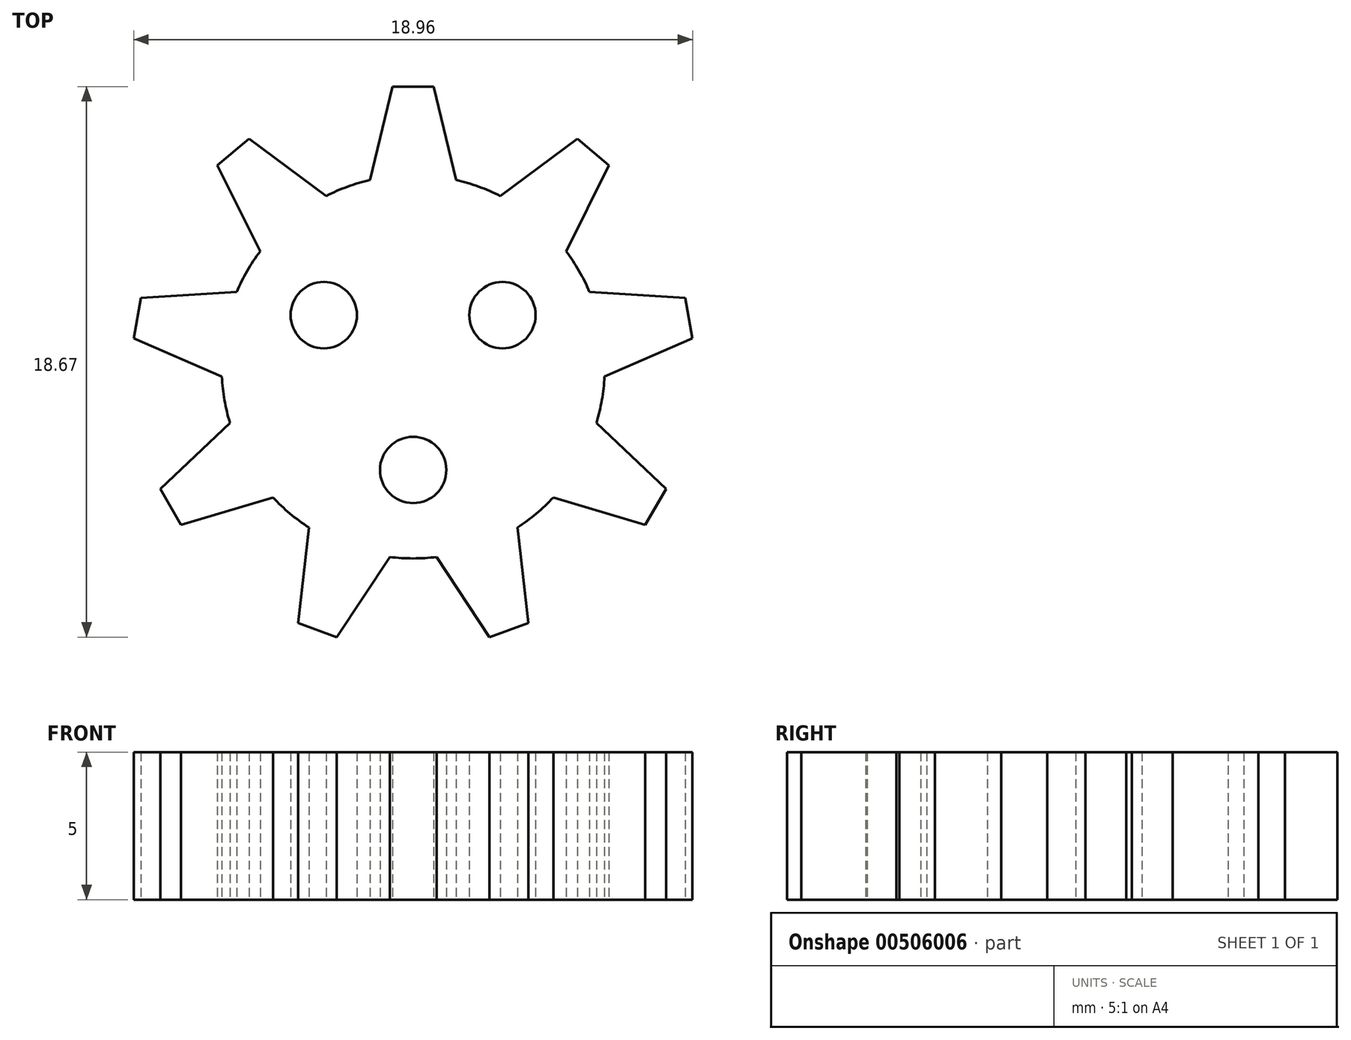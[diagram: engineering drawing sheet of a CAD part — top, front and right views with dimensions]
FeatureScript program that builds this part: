
annotation { "Feature Type Name" : "Feature", "Feature Type Description" : "" }
export const myFeature = defineFeature(function(context is Context, id is Id, definition is map)
    precondition{}
    {
        {
            var Q0;
            Q0=qCreatedBy(makeId("Top.planeOp"),FACE);
            var sketch = newSketch(context, id + "F0", { "sketchPlane" : qUnion([Q0])});
            skCircle(sketch, "E0", {"center": v(0, 0) * mm, "radius": 6.5 * mm});
            skLineSegment(sketch, "E1", {"start": v(0, 6.5) * mm, "end": v(0, 9.5) * mm});
            skLineSegment(sketch, "E2", {"start": v(0, 9.5) * mm, "end": v(0.7, 9.5) * mm});
            skLineSegment(sketch, "E3", {"start": v(0.7, 9.5) * mm, "end": v(1.46, 6.33) * mm});
            skLineSegment(sketch, "E4.MirrorCS", {"start": v(0, 9.5) * mm, "end": v(-0.7, 9.5) * mm});
            skLineSegment(sketch, "E5.MirrorCS", {"start": v(-0.7, 9.5) * mm, "end": v(-1.46, 6.33) * mm});
            skLineSegment(sketch, "E6.1.0", {"start": v(-6.64, 6.83) * mm, "end": v(-5.19, 3.91) * mm});
            skLineSegment(sketch, "E6.1.1", {"start": v(-6.1, 7.28) * mm, "end": v(-6.64, 6.83) * mm});
            skLineSegment(sketch, "E6.1.2", {"start": v(-6.1, 7.28) * mm, "end": v(-5.57, 7.73) * mm});
            skLineSegment(sketch, "E6.1.3", {"start": v(-5.57, 7.73) * mm, "end": v(-2.95, 5.8) * mm});
            skLineSegment(sketch, "E6.2.0", {"start": v(-9.48, 0.96) * mm, "end": v(-6.5, -0.34) * mm});
            skLineSegment(sketch, "E6.2.1", {"start": v(-9.36, 1.65) * mm, "end": v(-9.48, 0.96) * mm});
            skLineSegment(sketch, "E6.2.2", {"start": v(-9.36, 1.65) * mm, "end": v(-9.23, 2.34) * mm});
            skLineSegment(sketch, "E6.2.3", {"start": v(-9.23, 2.34) * mm, "end": v(-5.98, 2.54) * mm});
            skLineSegment(sketch, "E6.3.0", {"start": v(-7.88, -5.36) * mm, "end": v(-4.76, -4.43) * mm});
            skLineSegment(sketch, "E6.3.1", {"start": v(-8.23, -4.75) * mm, "end": v(-7.88, -5.36) * mm});
            skLineSegment(sketch, "E6.3.2", {"start": v(-8.23, -4.75) * mm, "end": v(-8.58, -4.14) * mm});
            skLineSegment(sketch, "E6.3.3", {"start": v(-8.58, -4.14) * mm, "end": v(-6.22, -1.9) * mm});
            skLineSegment(sketch, "E6.4.0", {"start": v(-2.6, -9.17) * mm, "end": v(-0.8, -6.45) * mm});
            skLineSegment(sketch, "E6.4.1", {"start": v(-3.25, -8.93) * mm, "end": v(-2.6, -9.17) * mm});
            skLineSegment(sketch, "E6.4.2", {"start": v(-3.25, -8.93) * mm, "end": v(-3.9, -8.69) * mm});
            skLineSegment(sketch, "E6.4.3", {"start": v(-3.9, -8.69) * mm, "end": v(-3.54, -5.45) * mm});
            skLineSegment(sketch, "E6.5.0", {"start": v(3.9, -8.69) * mm, "end": v(3.54, -5.45) * mm});
            skLineSegment(sketch, "E6.5.1", {"start": v(3.25, -8.93) * mm, "end": v(3.9, -8.69) * mm});
            skLineSegment(sketch, "E6.5.2", {"start": v(3.25, -8.93) * mm, "end": v(2.6, -9.17) * mm});
            skLineSegment(sketch, "E6.5.3", {"start": v(2.6, -9.17) * mm, "end": v(0.8, -6.45) * mm});
            skLineSegment(sketch, "E6.6.0", {"start": v(8.58, -4.14) * mm, "end": v(6.22, -1.9) * mm});
            skLineSegment(sketch, "E6.6.1", {"start": v(8.23, -4.75) * mm, "end": v(8.58, -4.14) * mm});
            skLineSegment(sketch, "E6.6.2", {"start": v(8.23, -4.75) * mm, "end": v(7.88, -5.36) * mm});
            skLineSegment(sketch, "E6.6.3", {"start": v(7.88, -5.36) * mm, "end": v(4.76, -4.43) * mm});
            skLineSegment(sketch, "E6.7.0", {"start": v(9.23, 2.34) * mm, "end": v(5.98, 2.54) * mm});
            skLineSegment(sketch, "E6.7.1", {"start": v(9.36, 1.65) * mm, "end": v(9.23, 2.34) * mm});
            skLineSegment(sketch, "E6.7.2", {"start": v(9.36, 1.65) * mm, "end": v(9.48, 0.96) * mm});
            skLineSegment(sketch, "E6.7.3", {"start": v(9.48, 0.96) * mm, "end": v(6.5, -0.34) * mm});
            skLineSegment(sketch, "E6.8.0", {"start": v(5.57, 7.73) * mm, "end": v(2.95, 5.8) * mm});
            skLineSegment(sketch, "E6.8.1", {"start": v(6.1, 7.28) * mm, "end": v(5.57, 7.73) * mm});
            skLineSegment(sketch, "E6.8.2", {"start": v(6.1, 7.28) * mm, "end": v(6.64, 6.83) * mm});
            skLineSegment(sketch, "E6.8.3", {"start": v(6.64, 6.83) * mm, "end": v(5.19, 3.91) * mm});
            skLineSegment(sketch, "E7", {"start": v(0, 0) * mm, "end": v(0, -3.5) * mm});
            skCircle(sketch, "E8", {"center": v(0, -3.5) * mm, "radius": 1.13 * mm});
            skCircle(sketch, "E9.1.0", {"center": v(3.03, 1.75) * mm, "radius": 1.13 * mm});
            skCircle(sketch, "E9.2.0", {"center": v(-3.03, 1.75) * mm, "radius": 1.13 * mm});
            skSolve(sketch);
        }
        {
            var Q0;
            Q0=makeQuery(id+"F0.imprint","IMPRINT",FACE,{"disambiguationData":[TD([[makeQuery(id+"F0.imprint","IMPRINT",EDGE,{"derivedFrom":sQuery(id+"F0.wireOp",EDGE,"E8")}),-1.0]])]});
            var Q1;
            {var subQ0=sQuery(id+"F0.wireOp",EDGE,"E6.4.0");Q1=makeQuery(id+"F0.imprint","IMPRINT",FACE,{"disambiguationData":[TD([[makeQuery(id+"F0.imprint","IMPRINT",EDGE,{"derivedFrom":subQ0}),1.0]])]});}
            var Q2;
            {var subQ0=sQuery(id+"F0.wireOp",EDGE,"E6.5.0");Q2=makeQuery(id+"F0.imprint","IMPRINT",FACE,{"disambiguationData":[TD([[makeQuery(id+"F0.imprint","IMPRINT",EDGE,{"derivedFrom":subQ0}),1.0]])]});}
            var Q3;
            {var subQ0=sQuery(id+"F0.wireOp",EDGE,"E6.6.0");Q3=makeQuery(id+"F0.imprint","IMPRINT",FACE,{"disambiguationData":[TD([[makeQuery(id+"F0.imprint","IMPRINT",EDGE,{"derivedFrom":subQ0}),1.0]])]});}
            var Q4;
            {var subQ0=sQuery(id+"F0.wireOp",EDGE,"E6.7.0");Q4=makeQuery(id+"F0.imprint","IMPRINT",FACE,{"disambiguationData":[TD([[makeQuery(id+"F0.imprint","IMPRINT",EDGE,{"derivedFrom":subQ0}),1.0]])]});}
            var Q5;
            {var subQ0=sQuery(id+"F0.wireOp",EDGE,"E6.8.0");Q5=makeQuery(id+"F0.imprint","IMPRINT",FACE,{"disambiguationData":[TD([[makeQuery(id+"F0.imprint","IMPRINT",EDGE,{"derivedFrom":subQ0}),1.0]])]});}
            var Q6;
            {var subQ0=sQuery(id+"F0.wireOp",EDGE,"E1");Q6=makeQuery(id+"F0.imprint","IMPRINT",FACE,{"disambiguationData":[TD([[makeQuery(id+"F0.imprint","IMPRINT",EDGE,{"derivedFrom":subQ0}),1.0]])]});}
            var Q7;
            {var subQ0=sQuery(id+"F0.wireOp",EDGE,"E1");Q7=makeQuery(id+"F0.imprint","IMPRINT",FACE,{"disambiguationData":[TD([[makeQuery(id+"F0.imprint","IMPRINT",EDGE,{"derivedFrom":subQ0}),-1.0]])]});}
            var Q8;
            {var subQ0=sQuery(id+"F0.wireOp",EDGE,"E6.1.0");Q8=makeQuery(id+"F0.imprint","IMPRINT",FACE,{"disambiguationData":[TD([[makeQuery(id+"F0.imprint","IMPRINT",EDGE,{"derivedFrom":subQ0}),1.0]])]});}
            var Q9;
            {var subQ0=sQuery(id+"F0.wireOp",EDGE,"E6.2.0");Q9=makeQuery(id+"F0.imprint","IMPRINT",FACE,{"disambiguationData":[TD([[makeQuery(id+"F0.imprint","IMPRINT",EDGE,{"derivedFrom":subQ0}),1.0]])]});}
            var Q10;
            {var subQ0=sQuery(id+"F0.wireOp",EDGE,"E6.3.0");Q10=makeQuery(id+"F0.imprint","IMPRINT",FACE,{"disambiguationData":[TD([[makeQuery(id+"F0.imprint","IMPRINT",EDGE,{"derivedFrom":subQ0}),1.0]])]});}
            extrude(context, id + "F1", {"entities" : qUnion([Q0, Q1, Q2, Q3, Q4, Q5, Q6, Q7, Q8, Q9, Q10]), "depth" : 5 * mm, "offsetDistance" : 25 * mm});
        }
    });
